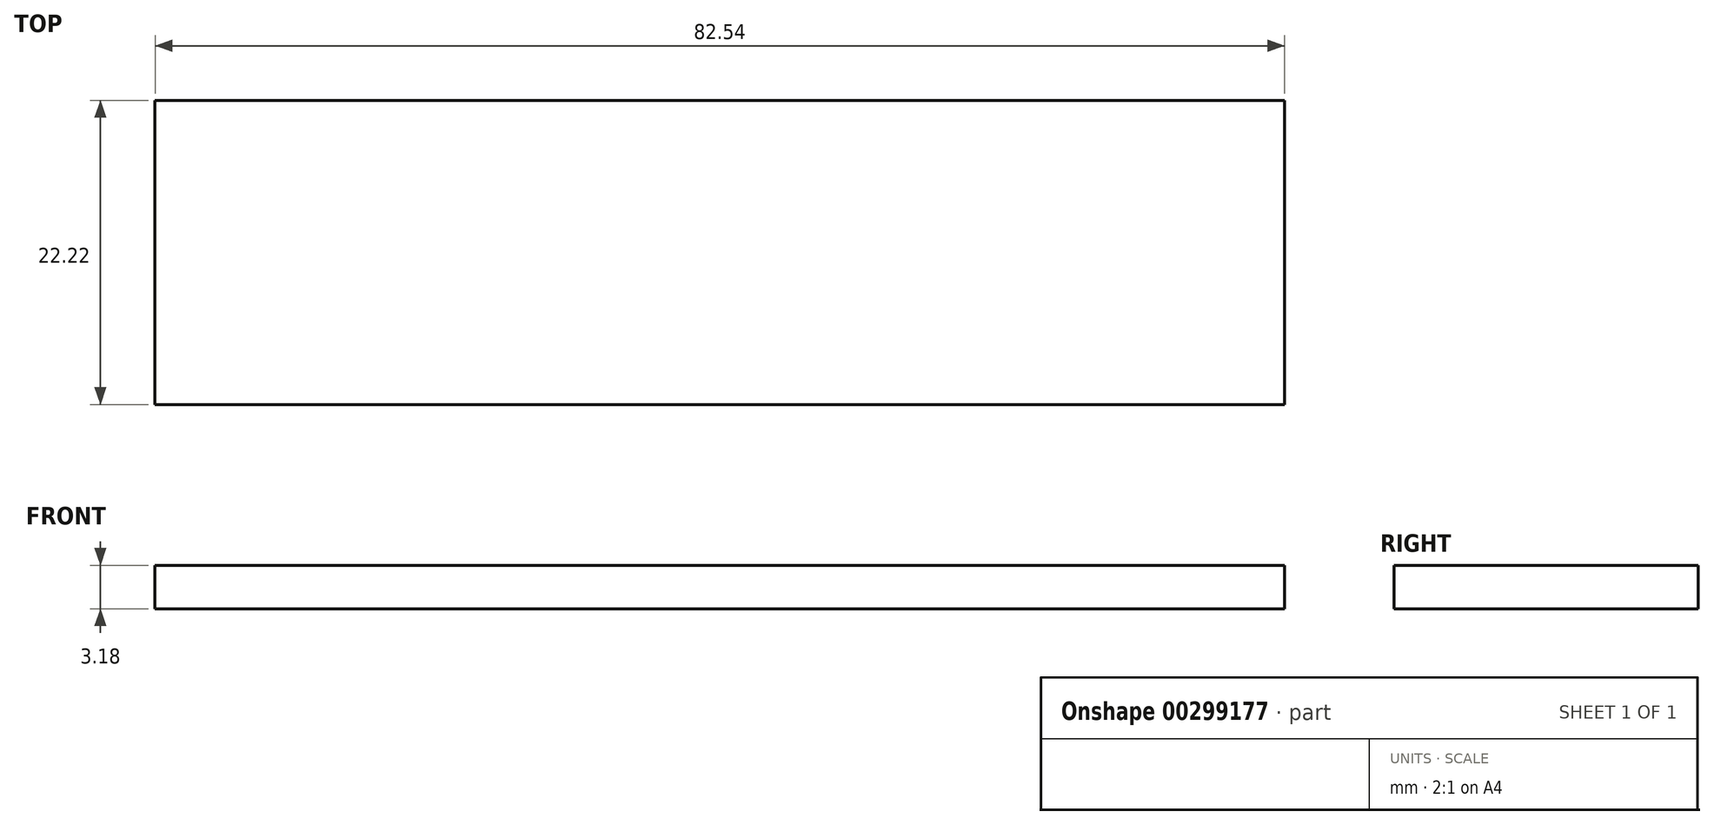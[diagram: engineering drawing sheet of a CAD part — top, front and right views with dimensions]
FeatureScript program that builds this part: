
annotation { "Feature Type Name" : "Feature", "Feature Type Description" : "" }
export const myFeature = defineFeature(function(context is Context, id is Id, definition is map)
    precondition{}
    {
        {
            var Q0;
            Q0=qCreatedBy(makeId("Front.planeOp"),FACE);
            var sketch = newSketch(context, id + "F0", { "sketchPlane" : qUnion([Q0])});
            skLineSegment(sketch, "E0.bottom", {"start": v(41.28, 1.59) * mm, "end": v(-41.28, 1.59) * mm});
            skLineSegment(sketch, "E0.top", {"start": v(41.28, -1.59) * mm, "end": v(-41.28, -1.59) * mm});
            skLineSegment(sketch, "E0.left", {"start": v(41.28, 1.59) * mm, "end": v(41.28, -1.59) * mm});
            skLineSegment(sketch, "E0.right", {"start": v(-41.28, 1.59) * mm, "end": v(-41.28, -1.59) * mm});
            skPoint(sketch, "E0.middle", {"position": v(0, 0) * mm});
            skSolve(sketch);
        }
        {
            var Q0;
            Q0 = qSketchRegion(id + "F0", true);
            extrude(context, id + "F1", {"entities" : qUnion([Q0]), "endBound" : BoundingType.SYMMETRIC, "depth" : 22.22 * mm});
        }
    });
